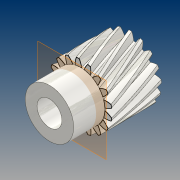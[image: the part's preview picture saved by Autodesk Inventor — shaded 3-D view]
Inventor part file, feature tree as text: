
AUTODESK INVENTOR PART (.ipt)
format: ipt  version: 2021 (Build 250183000, 183)  size: 985,600 bytes
history: native  units: mm (DEFAULTED — no unit token found)
features: sketch x7, extrude x6, plane x6, other x5, projected_geometry x4, loft x1, pattern_circular x1, mirror x1
ambient origin geometry x8: Origin, YZ Plane, XZ Plane, XY Plane, X Axis, Y Axis, Z Axis, Center Point
bodies: Solid1 (feature_tree)
feature tree (31):
  extrude  "Extrusion1"  Depth=25.0mm TaperAngle=0.0deg
  plane  "Work Plane2"
  plane  "Work Plane8"
  plane  "Work Plane9"
  other  "Spur Gear"
  sketch  "Sketch3"  dims[d16=40.0mm d17=0.0mm d34=1.847996mm]
  extrude  "Extrusion2"  Depth=10.0mm TaperAngle=0.0deg
  extrude  "Extrusion3"  Depth=1.847996mm TaperAngle=0.0deg
  plane  "Work Plane11"
  sketch  "Sketch4"  dims[d39=0.0mm d41=0.0mm]
  plane  "Work Plane12"
  sketch  "Sketch6"  dims[d43=40.0mm d46=40.0mm]
  sketch  "Sketch9"  dims[d47=0.0mm d48=0.0mm d49=10.0mm]
  sketch  "Sketch10"  dims[d51=10.0mm d52=0.0mm d53=17.5mm d54=0.0mm d55=3.5mm d64=4.0mm d65=2.0mm d66=2.5mm d67=0.0mm d68=7.75mm d69=0.0mm d70=6.5mm d71=0.0mm d72=20.0mm d73=90.0deg d75=3.0mm d76=0.0mm d77=90.0deg d78=0.0mm d79=90.0deg]
  loft  "Loft2"
  extrude  "Extrusion4"  Depth=40.0mm
  extrude  "Extrusion5"  Depth=10.0mm
  extrude  "Extrusion6"  Depth=17.5mm TaperAngle=0.0deg
  pattern_circular  "Circular Pattern1"  [2 undecoded]
  plane  "Work Plane13"
  mirror  "Mirror1"
  sketch  "Sketch1"  dims[d0=25.112479mm d1=25.0mm d2=0.0mm]
  sketch  "Sketch2"  dims[d3=22.613778mm d4=10.0mm d5=0.0mm]
  other  "Srf1"
  projected_geometry  "Projected Loop1"
  projected_geometry  "Projected Loop3"
  projected_geometry  "Projected Loop19"
  projected_geometry  "Projected Loop20"
  other  "Edges3"
  other  "Edges4"
  other  "Pitch Diameter"
note: 2 required parameter values undecoded (feature->parameter linkage not recoverable at this tier; creation-order binding heuristic only, values carry confidence <= 0.55)
